# Revit family: 60333_PRESTO_Barre en T diamètre 32 mm_FR
name_source: partatom
category: Appareils sanitaires
revit_build: Autodesk Revit 2018 (Build: 20190510_1515(x64)
units: mm (PartAtom-declared; Revit-internal decimal feet)

## family parameters
Basée sur le plan de construction = Non
Cote de connecteur circulaire = Utiliser le diamètre
Couper avec des vides une fois chargée = Non
Partagée = Non
Point de calcul de pièce = Non
Toujours verticalement = Oui
Type d'élément = Normal

## types (1)
- 60333 PRESTO Barre en T diamètre 32 mm
    Adresse = 7, RUE RACINE - 92542 MONTROUGE CEDEX FRANCE
    Description = Barre de douche en T, diamètre 32 mm. De type Presto réf. 60333 ou techniquement équivalent. En inox 304 brossé, de dimensions 500 x 1150 mm
    Fabricant = LES ROBINETS PRESTO S.A.
    Finition = - Tube acier inox 304
- Platine de fixation inox 304 soudée
- Finition poli satin
    Fonction = Dimensions :
- Diamètre : 32 mm
- Longueur x hauteur: 500x1150 mm

Matière et couleur de finition :
- Inox 304 brossé
- Platine de fixation, assemblage platine-barre vissée

Livré avec :
- Rosaces en inox permettant de dissimuler les vis de fixation
- Modèle en T

Normes / Agréments :
- Résistance au brouillard salin neutre (NSS) : 200 h selon NF ISO 9227
    Garantie = 3
    Hauteur = 1226 mm  [stored 4.02231 ft]
    Largeur = 82 mm  [stored 0.269029 ft]
    Lien CCTP = http://www.prestodatashare.com
    Lien fiche produit = http://www.prestodatashare.com
    Lien notice d'utilisation = http://www.prestodatashare.com
    Matériau = PRESTO métal
    Modèle = 60333 PRESTO BARRE DE DOUCHE EN T Ø32-INOX BROSSE
    Profondeur = 575 mm
    Reference = 60333
    URL = http://www.prestodatashare.com
    URL Fabricant = http://www.prestodatashare.com
    Variantes = 60333

note: [stored X ft] marks values corroborated as IEEE doubles in the binary element streams (Revit-internal decimal feet)
